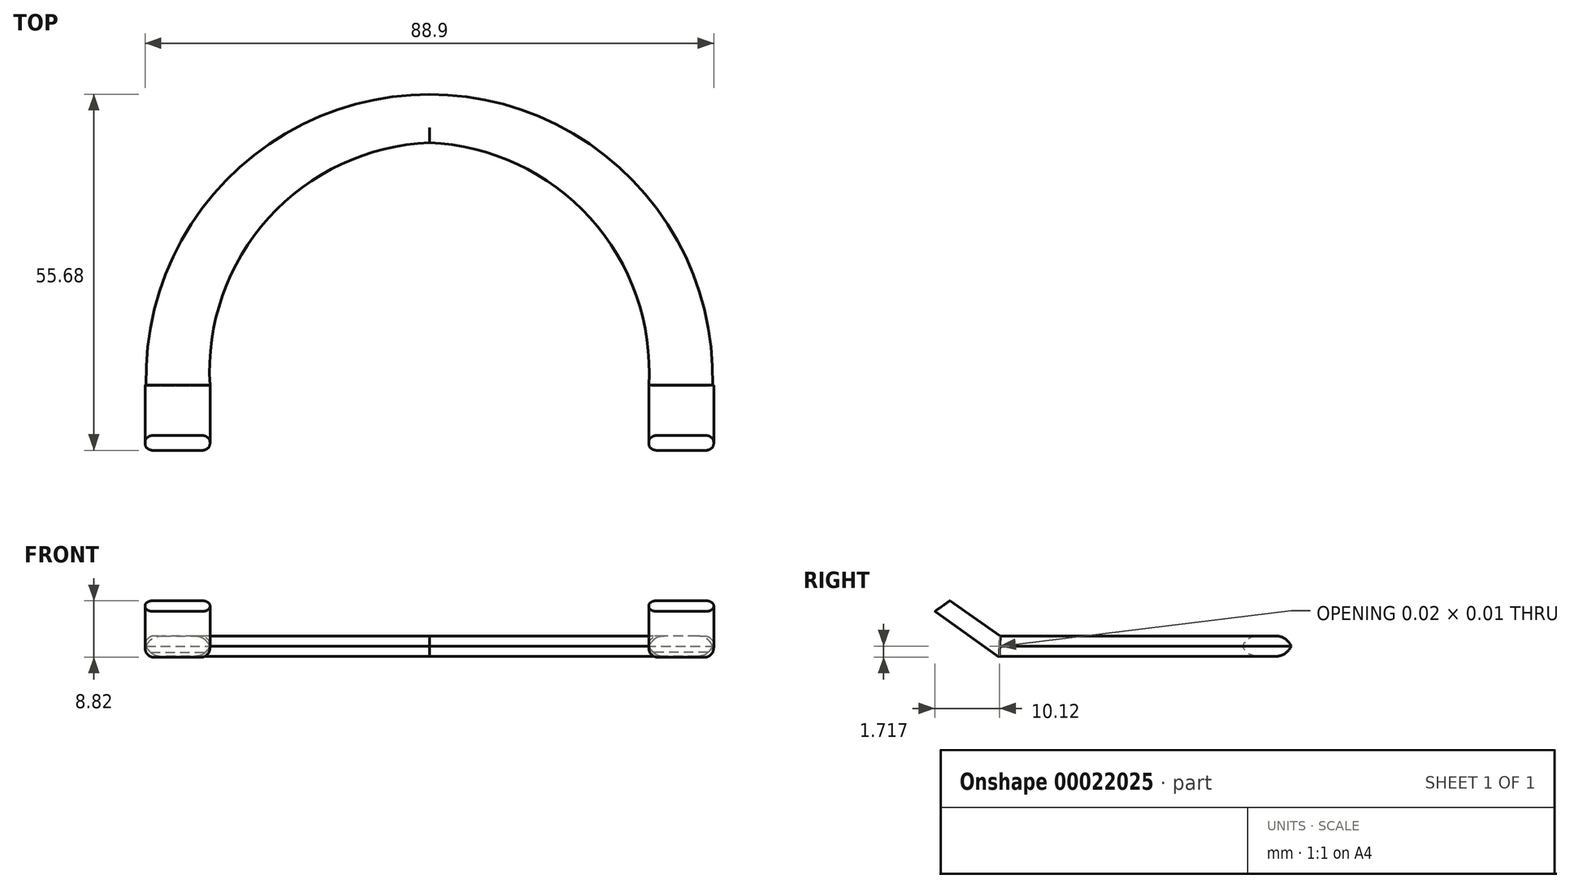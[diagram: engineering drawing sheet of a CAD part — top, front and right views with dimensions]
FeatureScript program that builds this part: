
annotation { "Feature Type Name" : "Feature", "Feature Type Description" : "" }
export const myFeature = defineFeature(function(context is Context, id is Id, definition is map)
    precondition{}
    {
        {
            var Q0;
            Q0=qCreatedBy(makeId("Top.planeOp"),FACE);
            var sketch = newSketch(context, id + "F0", { "sketchPlane" : qUnion([Q0])});
            skArc(sketch, "E0", {"start": v(0, 0) * mm, "mid": v(-44.45, 45.75) * mm, "end": v(-88.9, 0) * mm});
            skArc(sketch, "E1", {"start": v(-10.35, 0) * mm, "mid": v(-45.89, 37.85) * mm, "end": v(-81.43, 0) * mm});
            skLineSegment(sketch, "E2", {"start": v(-88.9, 0) * mm, "end": v(-81.43, 0) * mm});
            skLineSegment(sketch, "E3", {"start": v(-10.35, 0) * mm, "end": v(0, 0) * mm});
            skSolve(sketch);
        }
        {
            var Q0;
            Q0 = qSketchRegion(id + "F0", true);
            extrude(context, id + "F1", {"entities" : qUnion([Q0]), "depth" : 3.17 * mm});
        }
        {
            var Q0;
            Q0=makeQuery(id+"F1.opExtrude","CAP_EDGE",EDGE,{"disambiguationData":[OSD([sQuery(id+"F0.wireOp",EDGE,"E1")])],"isStart":false});
            var Q1;
            Q1=makeQuery(id+"F1.opExtrude","CAP_EDGE",EDGE,{"disambiguationData":[OSD([sQuery(id+"F0.wireOp",EDGE,"E0")])],"isStart":false});
            var Q2;
            Q2=makeQuery(id+"F1.opExtrude","CAP_EDGE",EDGE,{"disambiguationData":[OSD([sQuery(id+"F0.wireOp",EDGE,"E0")])],"isStart":true});
            var Q3;
            Q3=makeQuery(id+"F1.opExtrude","CAP_EDGE",EDGE,{"disambiguationData":[OSD([sQuery(id+"F0.wireOp",EDGE,"E1")])],"isStart":true});
            fillet(context, id + "F2", {"entities" : qUnion([Q0, Q1, Q2, Q3]), "radius" : 2.54 * mm, "tangentPropagation" : true, "allowEdgeOverflow" : false});
        }
        {
            var Q0;
            Q0=qCreatedBy(makeId("Right.planeOp"),FACE);
            var sketch = newSketch(context, id + "F3", { "sketchPlane" : qUnion([Q0])});
            skLineSegment(sketch, "E4", {"start": v(-0.04, -0.13) * mm, "end": v(-10.11, 7) * mm});
            skLineSegment(sketch, "E5", {"start": v(0.13, 3.15) * mm, "end": v(-7.76, 8.69) * mm});
            skLineSegment(sketch, "E6", {"start": v(-0.04, -0.13) * mm, "end": v(0.13, 3.15) * mm});
            skLineSegment(sketch, "E7", {"start": v(-7.76, 8.69) * mm, "end": v(-10.11, 7) * mm});
            skSolve(sketch);
        }
        {
            var Q0;
            Q0 = qSketchRegion(id + "F3", true);
            extrude(context, id + "F4", {"entities" : qUnion([Q0]), "operationType" : NewBodyOperationType.ADD, "oppositeDirection" : true, "depth" : 10.16 * mm});
        }
        {
            var Q0;
            Q0=makeQuery(id+"F4.opExtrude","CAP_EDGE",EDGE,{"disambiguationData":[OSD([sQuery(id+"F3.wireOp",EDGE,"E4")])],"isStart":true});
            var Q1;
            Q1=makeQuery(id+"F4.opExtrude","CAP_EDGE",EDGE,{"disambiguationData":[OSD([sQuery(id+"F3.wireOp",EDGE,"E5")])],"isStart":true});
            var Q2;
            Q2=makeQuery(id+"F4.opExtrude","CAP_EDGE",EDGE,{"disambiguationData":[OSD([sQuery(id+"F3.wireOp",EDGE,"E5")])],"isStart":false});
            var Q3;
            Q3=makeQuery(id+"F4.opExtrude","CAP_EDGE",EDGE,{"disambiguationData":[OSD([sQuery(id+"F3.wireOp",EDGE,"E4")])],"isStart":false});
            fillet(context, id + "F5", {"entities" : qUnion([Q0, Q1, Q2, Q3]), "radius" : 1.27 * mm, "tangentPropagation" : true, "allowEdgeOverflow" : false});
        }
        {
            var Q0;
            Q0=qCreatedBy(makeId("Right.planeOp"),FACE);
            cPlane(context, id + "F6", {"entities" : qUnion([Q0]), "cplaneType" : CPlaneType.OFFSET, "offset" : 44.45 * mm, "oppositeDirection" : true, "width" : 152.4 * mm, "height" : 152.4 * mm});
        }
        {
            var Q0;
            Q0=makeQuery(id+"F1.opExtrude","SWEPT_BODY",BODY,{"disambiguationData":[OSD([sQuery(id+"F0.wireOp",EDGE,"E0"),sQuery(id+"F0.wireOp",EDGE,"E1"),sQuery(id+"F0.wireOp",EDGE,"E2"),sQuery(id+"F0.wireOp",EDGE,"E3")])]});
            var Q1;
            Q1=qCreatedBy(id+"F6.planeOp",FACE);
            mirror(context, id + "F7", {"operationType" : NewBodyOperationType.ADD, "entities" : qUnion([Q0]), "mirrorPlane" : qUnion([Q1])});
        }
    });
